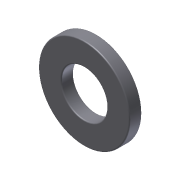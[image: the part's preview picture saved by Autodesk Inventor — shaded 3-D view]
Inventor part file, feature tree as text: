
AUTODESK INVENTOR PART (.ipt)
format: ipt  version: 2011 SP1 (Build 150282100, 282)  size: 105,984 bytes
history: native  units: in
note: dims shown in document units (in); Inventor stores cm internally (conversion verified against a paired STEP export)
features: fillet x2, extrude x1, sketch x1
ambient origin geometry x8: Origin, YZ Plane, XZ Plane, XY Plane, X Axis, Y Axis, Z Axis, Center Point
bodies: Solid1 (feature_tree)
feature tree (4):
  extrude  "Extrusion1"  Depth=0.812in
  fillet  "Fillet1"  Radius=0.11in
  fillet  "Fillet2"  Radius=0.01in
  sketch  "Sketch1"  dims[d0=0.406in d1=0.812in d2=0.11in d3=0.0in d4=0.01in d5=0.01in]
